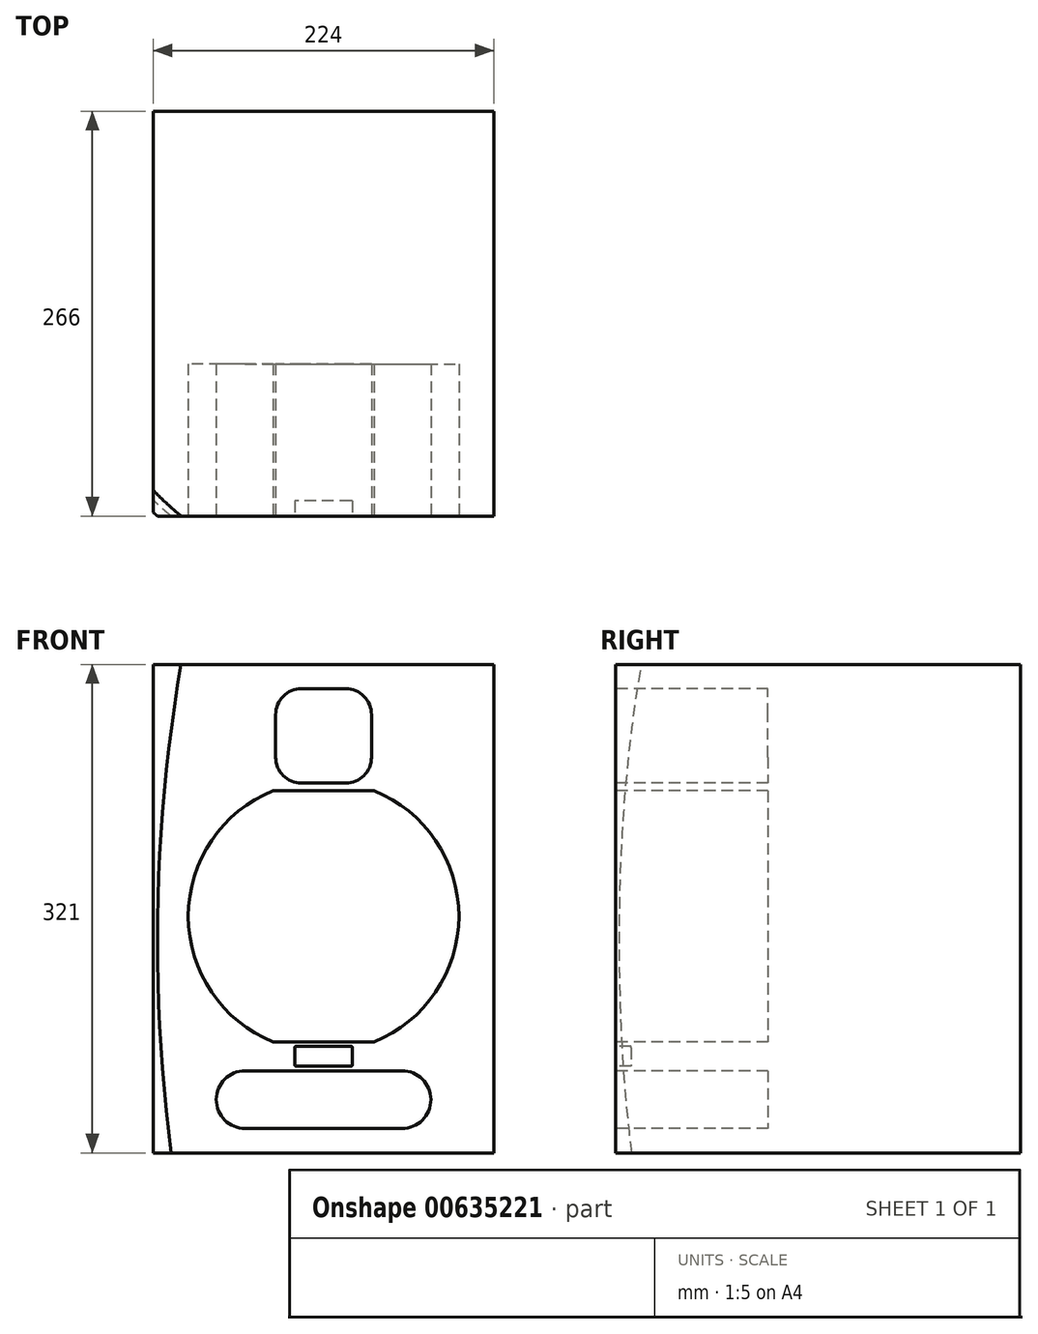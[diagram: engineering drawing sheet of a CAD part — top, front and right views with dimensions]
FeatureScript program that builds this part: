
annotation { "Feature Type Name" : "Feature", "Feature Type Description" : "" }
export const myFeature = defineFeature(function(context is Context, id is Id, definition is map)
    precondition{}
    {
        {
            var Q0;
            Q0=qCreatedBy(makeId("Top.planeOp"),FACE);
            var sketch = newSketch(context, id + "F0", { "sketchPlane" : qUnion([Q0])});
            skLineSegment(sketch, "E0.bottom", {"start": v(112, 133) * mm, "end": v(-112, 133) * mm});
            skLineSegment(sketch, "E0.top", {"start": v(112, -133) * mm, "end": v(-112, -133) * mm});
            skLineSegment(sketch, "E0.left", {"start": v(112, 133) * mm, "end": v(112, -133) * mm});
            skLineSegment(sketch, "E0.right", {"start": v(-112, 133) * mm, "end": v(-112, -133) * mm});
            skPoint(sketch, "E0.middle", {"position": v(0, 0) * mm});
            skSolve(sketch);
        }
        {
            var Q0;
            Q0 = qSketchRegion(id + "F0", true);
            extrude(context, id + "F1", {"entities" : qUnion([Q0]), "endBound" : BoundingType.SYMMETRIC, "depth" : 321 * mm, "offsetDistance" : 25.4 * mm});
        }
        {
            var Q0;
            Q0=makeQuery(id+"F1.opExtrude","SWEPT_FACE",FACE,{"disambiguationData":[OSD([sQuery(id+"F0.wireOp",EDGE,"E0.top")])]});
            var sketch = newSketch(context, id + "F2", { "sketchPlane" : qUnion([Q0])});
            skLineSegment(sketch, "E1.bottom", {"start": v(14.5, 82.5) * mm, "end": v(-14.5, 82.5) * mm});
            skLineSegment(sketch, "E1.top", {"start": v(14.5, 144.5) * mm, "end": v(-14.5, 144.5) * mm});
            skLineSegment(sketch, "E1.left", {"start": v(31.5, 99.5) * mm, "end": v(31.5, 127.5) * mm});
            skLineSegment(sketch, "E1.right", {"start": v(-31.5, 99.5) * mm, "end": v(-31.5, 127.5) * mm});
            skPoint(sketch, "E1.middle", {"position": v(0, 113.5) * mm});
            skPoint(sketch, "E2.visualSharp", {"position": v(-31.5, 144.5) * mm});
            skArc(sketch, "E2.filletArc", {"start": v(-14.5, 144.5) * mm, "mid": v(-26.52, 139.52) * mm, "end": v(-31.5, 127.5) * mm});
            skPoint(sketch, "E3.visualSharp", {"position": v(31.5, 144.5) * mm});
            skArc(sketch, "E3.filletArc", {"start": v(31.5, 127.5) * mm, "mid": v(26.52, 139.52) * mm, "end": v(14.5, 144.5) * mm});
            skPoint(sketch, "E4.visualSharp", {"position": v(31.5, 82.5) * mm});
            skArc(sketch, "E4.filletArc", {"start": v(14.5, 82.5) * mm, "mid": v(26.52, 87.48) * mm, "end": v(31.5, 99.5) * mm});
            skPoint(sketch, "E5.visualSharp", {"position": v(-31.5, 82.5) * mm});
            skArc(sketch, "E5.filletArc", {"start": v(-31.5, 99.5) * mm, "mid": v(-26.52, 87.48) * mm, "end": v(-14.5, 82.5) * mm});
            skSolve(sketch);
        }
        {
            var Q0;
            Q0 = qSketchRegion(id + "F2", true);
            extrude(context, id + "F3", {"entities" : qUnion([Q0]), "operationType" : NewBodyOperationType.REMOVE, "oppositeDirection" : true, "depth" : 100 * mm, "offsetDistance" : 25 * mm});
        }
        {
            var Q0;
            Q0=makeQuery(id+"F1.opExtrude","SWEPT_FACE",FACE,{"disambiguationData":[OSD([sQuery(id+"F0.wireOp",EDGE,"E0.top")])]});
            var sketch = newSketch(context, id + "F4", { "sketchPlane" : qUnion([Q0])});
            skArc(sketch, "E6", {"start": v(-33.12, 77.5) * mm, "mid": v(-88.9, -5) * mm, "end": v(-33.12, -87.5) * mm});
            skLineSegment(sketch, "E7", {"start": v(-33.12, 77.5) * mm, "end": v(33.12, 77.5) * mm});
            skLineSegment(sketch, "E8", {"start": v(-33.12, -87.5) * mm, "end": v(33.12, -87.5) * mm});
            skArc(sketch, "E9.trimOffspring", {"start": v(33.12, -87.5) * mm, "mid": v(88.9, -5) * mm, "end": v(33.12, 77.5) * mm});
            skSolve(sketch);
        }
        {
            var Q0;
            Q0 = qSketchRegion(id + "F4", true);
            extrude(context, id + "F5", {"entities" : qUnion([Q0]), "operationType" : NewBodyOperationType.REMOVE, "oppositeDirection" : true, "depth" : 100 * mm, "offsetDistance" : 25 * mm});
        }
        {
            var Q0;
            Q0=makeQuery(id+"F1.opExtrude","SWEPT_FACE",FACE,{"disambiguationData":[OSD([sQuery(id+"F0.wireOp",EDGE,"E0.top")])]});
            var sketch = newSketch(context, id + "F6", { "sketchPlane" : qUnion([Q0])});
            skLineSegment(sketch, "E10.bottom", {"start": v(18, -90.5) * mm, "end": v(-18, -90.5) * mm});
            skLineSegment(sketch, "E10.top", {"start": v(18, -103.5) * mm, "end": v(-18, -103.5) * mm});
            skLineSegment(sketch, "E10.left", {"start": v(19, -91.5) * mm, "end": v(19, -102.5) * mm});
            skLineSegment(sketch, "E10.right", {"start": v(-19, -91.5) * mm, "end": v(-19, -102.5) * mm});
            skPoint(sketch, "E10.middle", {"position": v(0, -97) * mm});
            skPoint(sketch, "E11.visualSharp", {"position": v(-19, -90.5) * mm});
            skArc(sketch, "E11.filletArc", {"start": v(-18, -90.5) * mm, "mid": v(-18.7, -90.8) * mm, "end": v(-19, -91.5) * mm});
            skPoint(sketch, "E12.visualSharp", {"position": v(19, -90.5) * mm});
            skArc(sketch, "E12.filletArc", {"start": v(19, -91.5) * mm, "mid": v(18.7, -90.8) * mm, "end": v(18, -90.5) * mm});
            skPoint(sketch, "E13.visualSharp", {"position": v(19, -103.5) * mm});
            skArc(sketch, "E13.filletArc", {"start": v(18, -103.5) * mm, "mid": v(18.7, -103.2) * mm, "end": v(19, -102.5) * mm});
            skPoint(sketch, "E14.visualSharp", {"position": v(-19, -103.5) * mm});
            skArc(sketch, "E14.filletArc", {"start": v(-19, -102.5) * mm, "mid": v(-18.7, -103.2) * mm, "end": v(-18, -103.5) * mm});
            skSolve(sketch);
        }
        {
            var Q0;
            Q0 = qSketchRegion(id + "F6", true);
            extrude(context, id + "F7", {"entities" : qUnion([Q0]), "operationType" : NewBodyOperationType.REMOVE, "oppositeDirection" : true, "depth" : 10 * mm, "offsetDistance" : 25 * mm});
        }
        {
            var Q0;
            Q0=makeQuery(id+"F1.opExtrude","SWEPT_FACE",FACE,{"disambiguationData":[OSD([sQuery(id+"F0.wireOp",EDGE,"E0.top")])]});
            var sketch = newSketch(context, id + "F8", { "sketchPlane" : qUnion([Q0])});
            skLineSegment(sketch, "E15", {"start": v(-51.5, -106.5) * mm, "end": v(51.5, -106.5) * mm});
            skLineSegment(sketch, "E16", {"start": v(-51.5, -144.5) * mm, "end": v(51.5, -144.5) * mm});
            skArc(sketch, "E17", {"start": v(-51.5, -106.5) * mm, "mid": v(-70.5, -125.5) * mm, "end": v(-51.5, -144.5) * mm});
            skArc(sketch, "E18", {"start": v(51.5, -144.5) * mm, "mid": v(70.5, -125.5) * mm, "end": v(51.5, -106.5) * mm});
            skSolve(sketch);
        }
        {
            var Q0;
            Q0 = qSketchRegion(id + "F8", true);
            extrude(context, id + "F9", {"entities" : qUnion([Q0]), "operationType" : NewBodyOperationType.REMOVE, "oppositeDirection" : true, "depth" : 100 * mm, "offsetDistance" : 25 * mm});
        }
        {
            var Q0;
            Q0=makeQuery(id+"F1.opExtrude","CAP_FACE",FACE,{"disambiguationData":[OSD([sQuery(id+"F0.wireOp",EDGE,"E0.bottom"),sQuery(id+"F0.wireOp",EDGE,"E0.top"),sQuery(id+"F0.wireOp",EDGE,"E0.left"),sQuery(id+"F0.wireOp",EDGE,"E0.right")])],"isStart":false});
            var sketch = newSketch(context, id + "F10", { "sketchPlane" : qUnion([Q0])});
            skLineSegment(sketch, "E19", {"start": v(-93.7, -133) * mm, "end": v(-112, -133) * mm});
            skLineSegment(sketch, "E20", {"start": v(-112, -133) * mm, "end": v(-112, -116) * mm});
            skArc(sketch, "E21", {"start": v(-112, -116) * mm, "mid": v(-103.12, -124.79) * mm, "end": v(-93.7, -133) * mm});
            skSolve(sketch);
        }
        {
            var Q0;
            Q0=makeQuery(id+"F1.opExtrude","SWEPT_FACE",FACE,{"disambiguationData":[OSD([sQuery(id+"F0.wireOp",EDGE,"E0.top")])]});
            var sketch = newSketch(context, id + "F11", { "sketchPlane" : qUnion([Q0])});
            skArc(sketch, "E22", {"start": v(-112, 160.5) * mm, "mid": v(-127.06, -6) * mm, "end": v(-116.71, -172.85) * mm});
            skSolve(sketch);
        }
        {
            var Q0;
            Q0=makeQuery(id+"F10.imprint","IMPRINT",FACE,{"disambiguationData":[TD([[makeQuery(id+"F10.imprint","IMPRINT",EDGE,{"derivedFrom":sQuery(id+"F10.wireOp",EDGE,"E19")}),-1.0]])]});
            var Q1;
            Q1=sQuery(id+"F11.wireOp",EDGE,"E22");
            sweep(context, id + "F12", {"operationType" : NewBodyOperationType.REMOVE, "profiles" : qUnion([Q0]), "path" : qUnion([Q1])});
        }
    });
